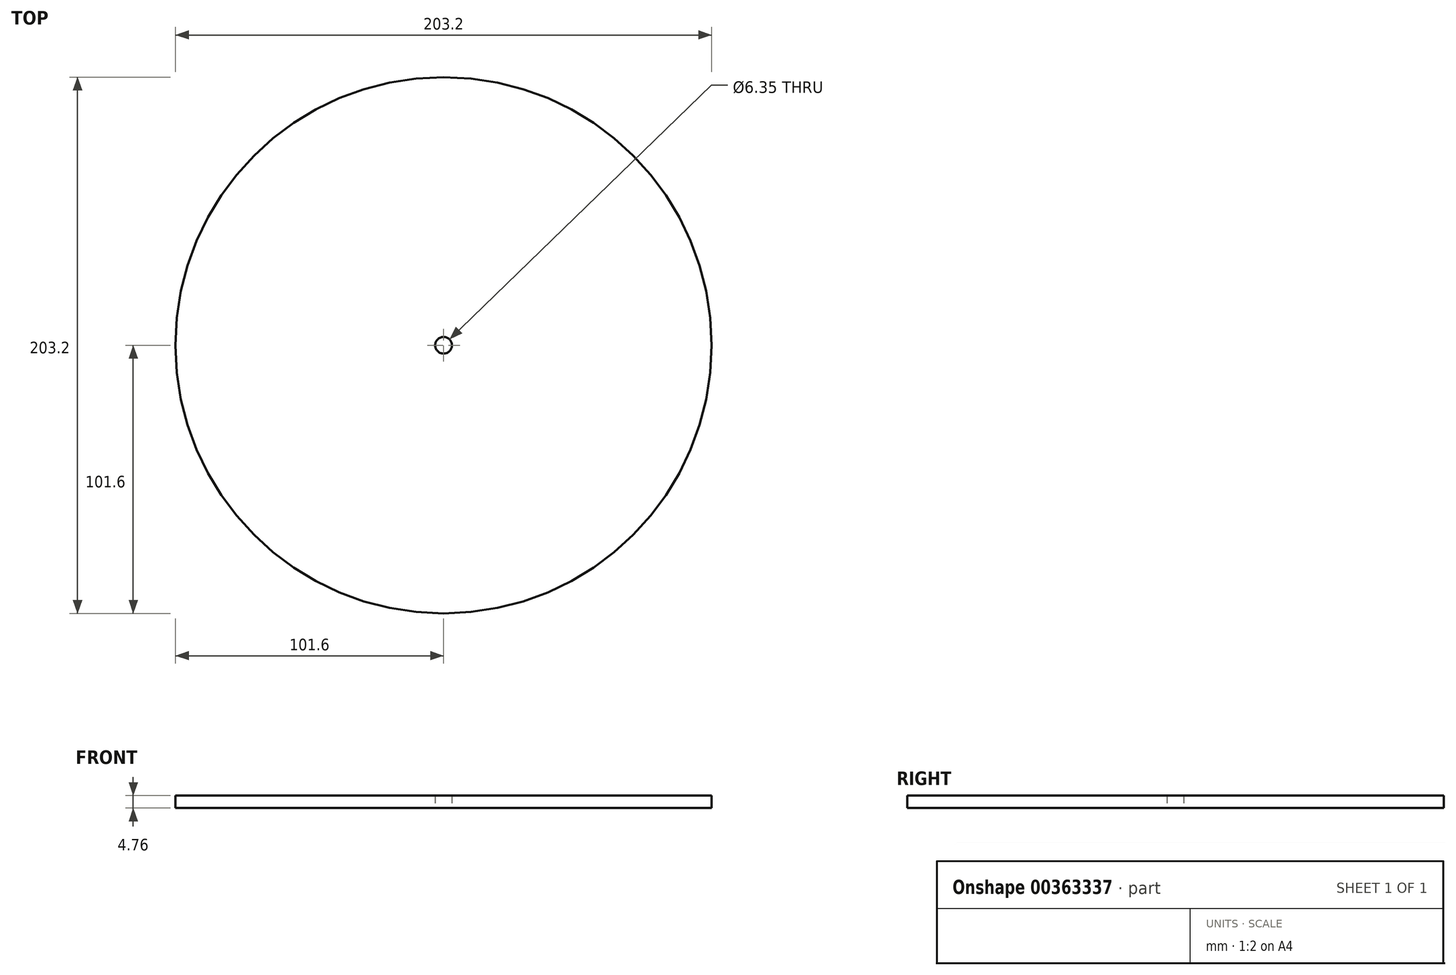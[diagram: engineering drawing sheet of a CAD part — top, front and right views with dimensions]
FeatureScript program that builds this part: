
annotation { "Feature Type Name" : "Feature", "Feature Type Description" : "" }
export const myFeature = defineFeature(function(context is Context, id is Id, definition is map)
    precondition{}
    {
        {
            var Q0;
            Q0=qCreatedBy(makeId("Top.planeOp"),FACE);
            var sketch = newSketch(context, id + "F0", { "sketchPlane" : qUnion([Q0])});
            skCircle(sketch, "E0", {"center": v(0, 0) * mm, "radius": 101.6 * mm});
            skCircle(sketch, "E1", {"center": v(0, 0) * mm, "radius": 3.18 * mm});
            skSolve(sketch);
        }
        {
            var Q0;
            Q0=makeQuery(id+"F0.imprint","IMPRINT",FACE,{"disambiguationData":[TD([[makeQuery(id+"F0.imprint","IMPRINT",EDGE,{"derivedFrom":sQuery(id+"F0.wireOp",EDGE,"E0")}),1.0]])]});
            extrude(context, id + "F1", {"entities" : qUnion([Q0]), "depth" : 4.76 * mm});
        }
    });
